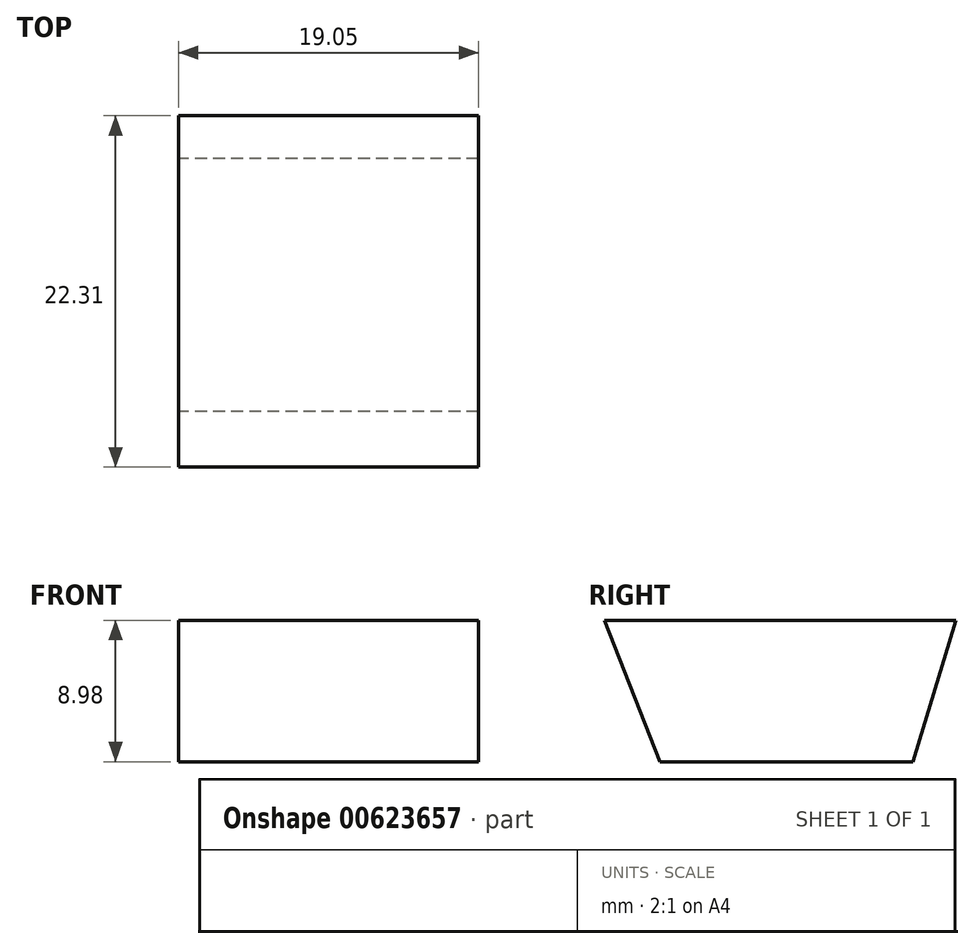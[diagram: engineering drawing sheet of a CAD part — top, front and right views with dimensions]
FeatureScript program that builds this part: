
annotation { "Feature Type Name" : "Feature", "Feature Type Description" : "" }
export const myFeature = defineFeature(function(context is Context, id is Id, definition is map)
    precondition{}
    {
        {
            var Q0;
            Q0=qCreatedBy(makeId("Right.planeOp"),FACE);
            var sketch = newSketch(context, id + "F0", { "sketchPlane" : qUnion([Q0])});
            skLineSegment(sketch, "E0", {"start": v(-13.74, -0.14) * mm, "end": v(-10.2, -9.12) * mm});
            skLineSegment(sketch, "E1", {"start": v(-10.2, -9.12) * mm, "end": v(5.85, -9.12) * mm});
            skLineSegment(sketch, "E2", {"start": v(5.85, -9.12) * mm, "end": v(8.57, -0.14) * mm});
            skLineSegment(sketch, "E3", {"start": v(8.57, -0.14) * mm, "end": v(-13.74, -0.14) * mm});
            skSolve(sketch);
        }
        {
            var Q0;
            Q0=makeQuery(id+"F0.imprint","IMPRINT",FACE,{"disambiguationData":[TD([[makeQuery(id+"F0.imprint","IMPRINT",EDGE,{"derivedFrom":sQuery(id+"F0.wireOp",EDGE,"E0")}),1.0]])]});
            extrude(context, id + "F1", {"entities" : qUnion([Q0]), "depth" : 19.05 * mm, "offsetDistance" : 25.4 * mm});
        }
    });
